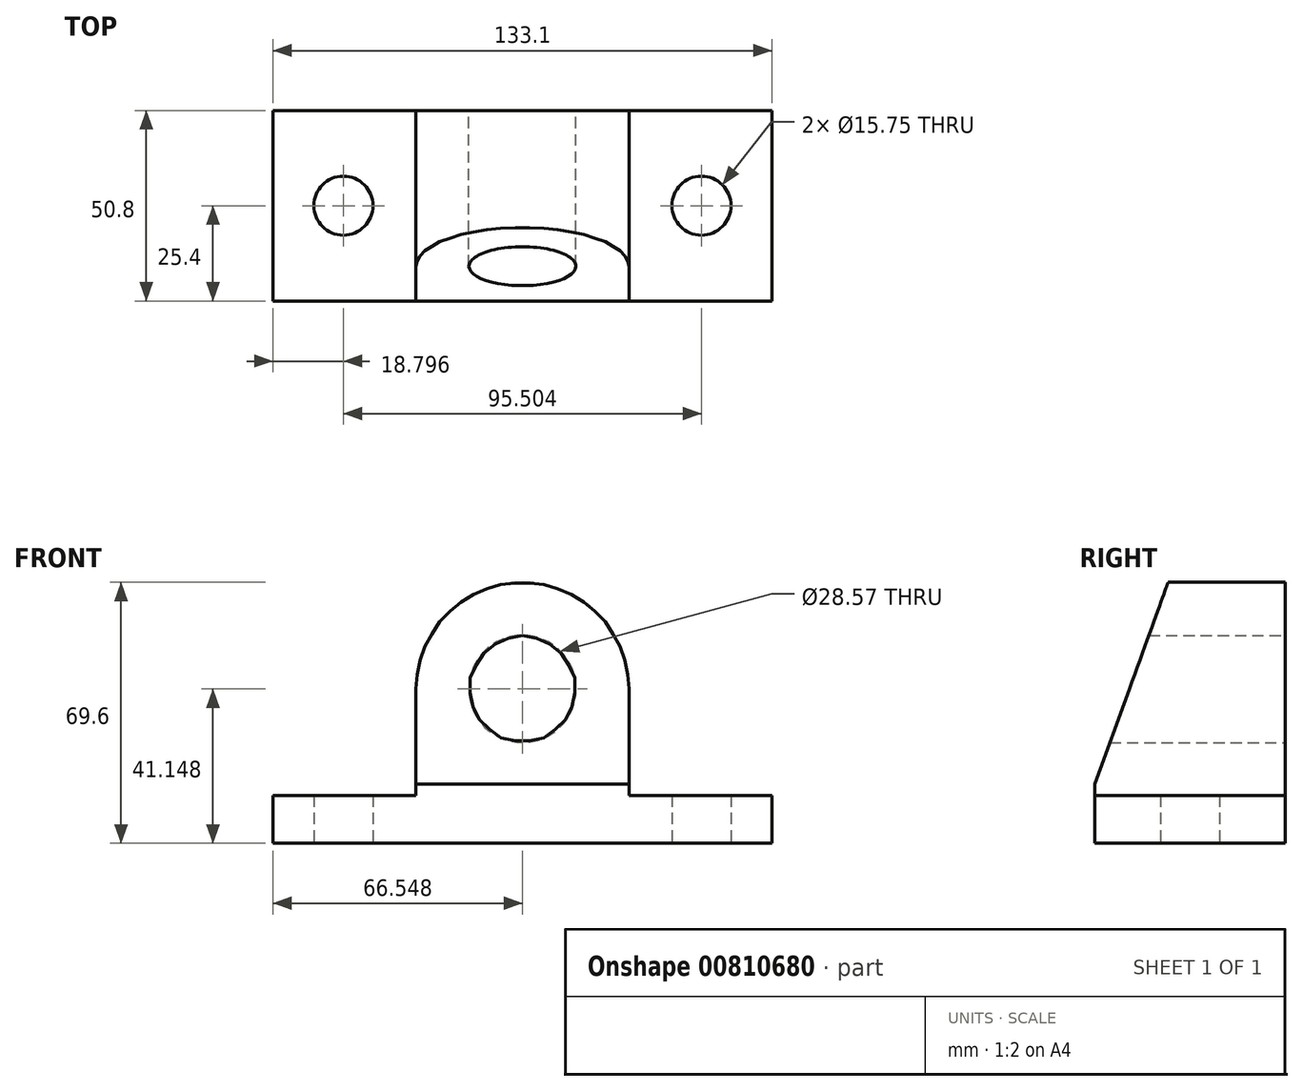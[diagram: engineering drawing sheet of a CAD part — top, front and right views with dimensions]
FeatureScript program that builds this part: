
annotation { "Feature Type Name" : "Feature", "Feature Type Description" : "" }
export const myFeature = defineFeature(function(context is Context, id is Id, definition is map)
    precondition{}
    {
        {
            var Q0;
            Q0=qCreatedBy(makeId("Top.planeOp"),FACE);
            var sketch = newSketch(context, id + "F0", { "sketchPlane" : qUnion([Q0])});
            skLineSegment(sketch, "E0.bottom", {"start": v(0, 0) * mm, "end": v(133.1, 0) * mm});
            skLineSegment(sketch, "E0.top", {"start": v(0, -50.8) * mm, "end": v(133.1, -50.8) * mm});
            skLineSegment(sketch, "E0.left", {"start": v(0, 0) * mm, "end": v(0, -50.8) * mm});
            skLineSegment(sketch, "E0.right", {"start": v(133.1, 0) * mm, "end": v(133.1, -50.8) * mm});
            skSolve(sketch);
        }
        {
            var Q0;
            Q0=makeQuery(id+"F0.imprint","IMPRINT",FACE,{"disambiguationData":[TD([[makeQuery(id+"F0.imprint","IMPRINT",EDGE,{"derivedFrom":sQuery(id+"F0.wireOp",EDGE,"E0.bottom")}),-1.0]])]});
            extrude(context, id + "F1", {"entities" : qUnion([Q0]), "depth" : 12.7 * mm, "offsetDistance" : 25.4 * mm});
        }
        {
            var Q0;
            Q0=makeQuery(id+"F1.opExtrude","CAP_FACE",FACE,{"disambiguationData":[OSD([sQuery(id+"F0.wireOp",EDGE,"E0.bottom"),sQuery(id+"F0.wireOp",EDGE,"E0.top"),sQuery(id+"F0.wireOp",EDGE,"E0.left"),sQuery(id+"F0.wireOp",EDGE,"E0.right")])],"isStart":false});
            var sketch = newSketch(context, id + "F2", { "sketchPlane" : qUnion([Q0])});
            skLineSegment(sketch, "E1.bottom", {"start": v(38.1, 0) * mm, "end": v(95, 0) * mm});
            skLineSegment(sketch, "E1.top", {"start": v(38.1, -50.8) * mm, "end": v(95, -50.8) * mm});
            skLineSegment(sketch, "E1.left", {"start": v(38.1, 0) * mm, "end": v(38.1, -50.8) * mm});
            skLineSegment(sketch, "E1.right", {"start": v(95, 0) * mm, "end": v(95, -50.8) * mm});
            skSolve(sketch);
        }
        {
            var Q0;
            Q0=makeQuery(id+"F2.imprint","IMPRINT",FACE,{"disambiguationData":[TD([[makeQuery(id+"F2.imprint","IMPRINT",EDGE,{"derivedFrom":sQuery(id+"F2.wireOp",EDGE,"E1.bottom")}),-1.0]])]});
            extrude(context, id + "F3", {"entities" : qUnion([Q0]), "operationType" : NewBodyOperationType.ADD, "depth" : 56.9 * mm, "offsetDistance" : 25.4 * mm});
        }
        {
            var Q0;
            Q0=makeQuery(id+"F3.opExtrude","CAP_EDGE",EDGE,{"disambiguationData":[OSD([sQuery(id+"F2.wireOp",EDGE,"E1.top")])],"isStart":false});
            chamfer(context, id + "F4", {"entities" : qUnion([Q0]), "chamferType" : ChamferType.TWO_OFFSETS, "width1" : 19.6 * mm, "oppositeDirection" : false, "width2" : 53.85 * mm, "tangentPropagation" : true});
        }
        {
            var Q0;
            Q0=makeQuery(id+"F3.boolean.opBoolean","MERGE",FACE,{"derivedFrom":[makeQuery(id+"F1.opExtrude","SWEPT_FACE",FACE,{"disambiguationData":[OSD([sQuery(id+"F0.wireOp",EDGE,"E0.bottom")])]}),makeQuery(id+"F3.opExtrude","SWEPT_FACE",FACE,{"disambiguationData":[OSD([sQuery(id+"F2.wireOp",EDGE,"E1.bottom")])]})]});
            var sketch = newSketch(context, id + "F5", { "sketchPlane" : qUnion([Q0])});
            skCircle(sketch, "E2", {"center": v(-66.55, 41.15) * mm, "radius": 14.29 * mm});
            skSolve(sketch);
        }
        {
            var Q0;
            Q0=makeQuery(id+"F5.imprint","IMPRINT",FACE,{"disambiguationData":[TD([[makeQuery(id+"F5.imprint","IMPRINT",EDGE,{"derivedFrom":sQuery(id+"F5.wireOp",EDGE,"E2")}),1.0]])]});
            extrude(context, id + "F6", {"entities" : qUnion([Q0]), "operationType" : NewBodyOperationType.REMOVE, "oppositeDirection" : true, "depth" : 50.8 * mm, "offsetDistance" : 25.4 * mm});
        }
        {
            var Q0;
            Q0=makeQuery(id+"F3.opExtrude","CAP_EDGE",EDGE,{"disambiguationData":[OSD([sQuery(id+"F2.wireOp",EDGE,"E1.right")])],"isStart":false});
            var Q1;
            Q1=makeQuery(id+"F3.opExtrude","CAP_EDGE",EDGE,{"disambiguationData":[OSD([sQuery(id+"F2.wireOp",EDGE,"E1.left")])],"isStart":false});
            fillet(context, id + "F7", {"entities" : qUnion([Q0, Q1]), "radius" : 28.45 * mm, "tangentPropagation" : true, "allowEdgeOverflow" : false});
        }
        {
            var Q0;
            Q0=makeQuery(id+"F1.opExtrude","CAP_FACE",FACE,{"disambiguationData":[OSD([sQuery(id+"F0.wireOp",EDGE,"E0.bottom"),sQuery(id+"F0.wireOp",EDGE,"E0.top"),sQuery(id+"F0.wireOp",EDGE,"E0.left"),sQuery(id+"F0.wireOp",EDGE,"E0.right")])],"isStart":true});
            var sketch = newSketch(context, id + "F8", { "sketchPlane" : qUnion([Q0])});
            skCircle(sketch, "E3", {"center": v(114.3, 25.4) * mm, "radius": 7.87 * mm});
            skSolve(sketch);
        }
        {
            var Q0;
            Q0=makeQuery(id+"F8.imprint","IMPRINT",FACE,{"disambiguationData":[TD([[makeQuery(id+"F8.imprint","IMPRINT",EDGE,{"derivedFrom":sQuery(id+"F8.wireOp",EDGE,"E3")}),-1.0]])]});
            var sketch = newSketch(context, id + "F9", { "sketchPlane" : qUnion([Q0])});
            skCircle(sketch, "E4", {"center": v(18.8, 25.4) * mm, "radius": 7.87 * mm});
            skSolve(sketch);
        }
        {
            var Q0;
            Q0=makeQuery(id+"F9.imprint","IMPRINT",FACE,{"disambiguationData":[TD([[makeQuery(id+"F9.imprint","IMPRINT",EDGE,{"derivedFrom":sQuery(id+"F9.wireOp",EDGE,"E4")}),1.0]])]});
            var Q1;
            Q1=makeQuery(id+"F8.imprint","IMPRINT",FACE,{"disambiguationData":[TD([[makeQuery(id+"F8.imprint","IMPRINT",EDGE,{"derivedFrom":sQuery(id+"F8.wireOp",EDGE,"E3")}),1.0]])]});
            extrude(context, id + "F10", {"entities" : qUnion([Q0, Q1]), "operationType" : NewBodyOperationType.REMOVE, "oppositeDirection" : true, "depth" : 25.4 * mm, "offsetDistance" : 25.4 * mm});
        }
    });
